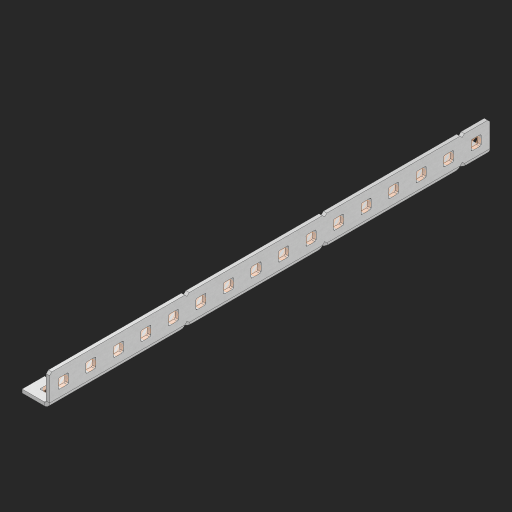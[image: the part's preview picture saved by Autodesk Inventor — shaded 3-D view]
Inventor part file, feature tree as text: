
AUTODESK INVENTOR PART (.ipt)
format: ipt  version: 2023 (Build 270158000, 158)  size: 883,712 bytes
history: native  units: in
note: dims shown in document units (in); Inventor stores cm internally (conversion verified against a paired STEP export)
features: other x196, extrude x46, sheet_metal_op x11, sketch x10, pattern_linear x2, mirror x1, chamfer x1
ambient origin geometry x8: Origin, YZ Plane, XZ Plane, XY Plane, X Axis, Y Axis, Z Axis, Center Point
bodies: Solid1 (feature_tree), Body (feature_tree)
feature tree (267):
  other  "Alu Half C 1x2x1x16"
  other  "Table"
  other  "Alu C 1x2x1x35"
  other  "Alu C 1x2x1x34"
  other  "Alu C 1x2x1x33"
  other  "Alu C 1x2x1x32"
  other  "Alu C 1x2x1x31"
  other  "Alu C 1x2x1x30"
  other  "Alu C 1x2x1x29"
  other  "Alu C 1x2x1x28"
  other  "Alu C 1x2x1x27"
  other  "Alu C 1x2x1x26"
  other  "Alu C 1x2x1x25"
  other  "Alu C 1x2x1x24"
  other  "Alu C 1x2x1x23"
  other  "Alu C 1x2x1x22"
  other  "Alu C 1x2x1x21"
  other  "Alu C 1x2x1x20"
  other  "Alu C 1x2x1x19"
  other  "Alu C 1x2x1x18"
  other  "Alu C 1x2x1x17"
  other  "Alu C 1x2x1x16"
  other  "Alu C 1x2x1x15"
  other  "Alu C 1x2x1x14"
  other  "Alu C 1x2x1x13"
  other  "Alu C 1x2x1x12"
  other  "Alu C 1x2x1x11"
  other  "Alu C 1x2x1x10"
  other  "Alu C 1x2x1x9"
  other  "Alu C 1x2x1x8"
  other  "Alu C 1x2x1x7"
  other  "Alu C 1x2x1x6"
  other  "Alu C 1x2x1x5"
  other  "Alu C 1x2x1x4"
  other  "Alu C 1x2x1x3"
  other  "Alu C 1x2x1x2"
  other  "Alu C 1x2x1x1"
  other  "Steel C 1x2x1x35"
  other  "Steel C 1x2x1x34"
  other  "Steel C 1x2x1x33"
  other  "Steel C 1x2x1x32"
  other  "Steel C 1x2x1x31"
  other  "Steel C 1x2x1x30"
  other  "Steel C 1x2x1x29"
  other  "Steel C 1x2x1x28"
  other  "Steel C 1x2x1x27"
  other  "Steel C 1x2x1x26"
  other  "Steel C 1x2x1x25"
  other  "Steel C 1x2x1x24"
  other  "Steel C 1x2x1x23"
  other  "Steel C 1x2x1x22"
  other  "Steel C 1x2x1x21"
  other  "Steel C 1x2x1x20"
  other  "Steel C 1x2x1x19"
  other  "Steel C 1x2x1x18"
  other  "Steel C 1x2x1x17"
  other  "Steel C 1x2x1x16"
  other  "Steel C 1x2x1x15"
  other  "Steel C 1x2x1x14"
  other  "Steel C 1x2x1x13"
  other  "Steel C 1x2x1x12"
  other  "Steel C 1x2x1x11"
  other  "Steel C 1x2x1x10"
  other  "Steel C 1x2x1x9"
  other  "Steel C 1x2x1x8"
  other  "Steel C 1x2x1x7"
  other  "Steel C 1x2x1x6"
  other  "Steel C 1x2x1x5"
  other  "Steel C 1x2x1x4"
  other  "Steel C 1x2x1x3"
  other  "Steel C 1x2x1x2"
  other  "Steel C 1x2x1x1"
  other  "Alu Half C 1x2x1x35"
  other  "Alu Half C 1x2x1x34"
  other  "Alu Half C 1x2x1x33"
  other  "Alu Half C 1x2x1x32"
  other  "Alu Half C 1x2x1x31"
  other  "Alu Half C 1x2x1x30"
  other  "Alu Half C 1x2x1x29"
  other  "Alu Half C 1x2x1x28"
  other  "Alu Half C 1x2x1x27"
  other  "Alu Half C 1x2x1x26"
  other  "Alu Half C 1x2x1x25"
  other  "Alu Half C 1x2x1x24"
  other  "Alu Half C 1x2x1x23"
  other  "Alu Half C 1x2x1x22"
  other  "Alu Half C 1x2x1x21"
  other  "Alu Half C 1x2x1x20"
  other  "Alu Half C 1x2x1x19"
  other  "Alu Half C 1x2x1x18"
  other  "Alu Half C 1x2x1x17"
  other  "Alu Half C 1x2x1x15"
  other  "Alu Half C 1x2x1x14"
  other  "Alu Half C 1x2x1x13"
  other  "Alu Half C 1x2x1x12"
  other  "Alu Half C 1x2x1x11"
  other  "Alu Half C 1x2x1x10"
  other  "Alu Half C 1x2x1x9"
  other  "Alu Half C 1x2x1x8"
  other  "Alu Half C 1x2x1x7"
  other  "Alu Half C 1x2x1x6"
  other  "Alu Half C 1x2x1x5"
  other  "Alu Half C 1x2x1x4"
  other  "Alu Half C 1x2x1x3"
  other  "Alu Half C 1x2x1x2"
  other  "Alu Half C 1x2x1x1"
  other  "Steel Half C 1x2x1x35"
  other  "Steel Half C 1x2x1x34"
  other  "Steel Half C 1x2x1x33"
  other  "Steel Half C 1x2x1x32"
  other  "Steel Half C 1x2x1x31"
  other  "Steel Half C 1x2x1x30"
  other  "Steel Half C 1x2x1x29"
  other  "Steel Half C 1x2x1x28"
  other  "Steel Half C 1x2x1x27"
  other  "Steel Half C 1x2x1x26"
  other  "Steel Half C 1x2x1x25"
  other  "Steel Half C 1x2x1x24"
  other  "Steel Half C 1x2x1x23"
  other  "Steel Half C 1x2x1x22"
  other  "Steel Half C 1x2x1x21"
  other  "Steel Half C 1x2x1x20"
  other  "Steel Half C 1x2x1x19"
  other  "Steel Half C 1x2x1x18"
  other  "Steel Half C 1x2x1x17"
  other  "Steel Half C 1x2x1x16"
  other  "Steel Half C 1x2x1x15"
  other  "Steel Half C 1x2x1x14"
  other  "Steel Half C 1x2x1x13"
  other  "Steel Half C 1x2x1x12"
  other  "Steel Half C 1x2x1x11"
  other  "Steel Half C 1x2x1x10"
  other  "Steel Half C 1x2x1x9"
  other  "Steel Half C 1x2x1x8"
  other  "Steel Half C 1x2x1x7"
  other  "Steel Half C 1x2x1x6"
  other  "Steel Half C 1x2x1x5"
  other  "Steel Half C 1x2x1x4"
  other  "Steel Half C 1x2x1x3"
  other  "Steel Half C 1x2x1x2"
  other  "Steel Half C 1x2x1x1"
  sheet_metal_op  "Flanges"
  other  "Flange Pattern Plane"
  other  "Flange Pattern Sketch"
  sheet_metal_op  "Flange Pattern"
  sheet_metal_op  "Body Pattern"
  pattern_linear  "Center Pattern"  Spacing1=0.0625in  [1 undecoded]
  other  "Arc Length"
  mirror  "Notch Mirror"
  pattern_linear  "Notch Pattern"  Spacing1=0.182in  [1 undecoded]
  chamfer  "End Chamfer"
  extrude  "Half Cut"  Depth=0.02in
  sketch  "Sketch1"  dims[d0=1.0in]
  other  "Plate1"
  sketch  "Sketch2"  dims[d1=8.0in]
  other  "Plate2"
  sheet_metal_op  "Bend1"
  sheet_metal_op  "Corner1"
  sketch  "Sketch3"  dims[d2=0.0625in]
  sketch  "Sketch7"  dims[d3=0.0625in]
  other  "Srf1"
  other  "Srf2"
  sketch  "Sketch8"  dims[d4=0.0312in]
  sketch  "Sketch9"  dims[d5=0.125in]
  other  "Srf91"
  sheet_metal_op  "Body Pattern Sketch"
  other  "Srf92"
  sketch  "Sketch13"  dims[d6=0.0625in]
  sketch  "Sketch14"  dims[d7=0.5in d8=90.0deg d9=0.0312in]
  sketch  "Sketch15"  dims[d10=0.25in]
  sketch  "Sketch16"  dims[d11=0.0625in d12=0.0625in d16=0.182in d17=0.02in d18=0.0625in d19=0.0in d20=0.25in d21=0.25in d38=6.2992in d40=0.5in d41=0.3937in d43=1.0in d46=0.172in d47=1.0in d48=0.0in d49=0.182in d50=0.02in d51=0.25in d52=0.25in d53=0.0625in d54=0.0in d55=0.172in d56=1.0in d57=0.0in d58=0.25in d60=6.2992in d62=0.5in d63=0.3937in d65=0.5in d85=0.1473in d86=0.1782in d88=0.04in d89=0.0625in d90=0.0in d91=0.04in d92=0.0491in d95=2.5in d96=0.04in d97=0.25in d98=45.0deg d99=0.25in d100=0.5in d101=0.0in d102=2.497in d106=0.182in d107=0.02in d108=0.5in d109=0.5in d110=0.0625in d111=0.0in d112=0.172in d113=0.5in d114=0.0in d117=0.5in d118=0.5in d119=0.5in]
  other  "Srf786"
  other  "Srf823"
  other  "Srf824"
  other  "Srf825"
  other  "Srf826"
  other  "Srf827"
  other  "Srf828"
  other  "Srf829"
  other  "Srf856"
  other  "Srf857"
  other  "Srf858"
  other  "Srf859"
  other  "Srf860"
  other  "Srf861"
  other  "Srf862"
  other  "Srf889"
  other  "Srf890"
  other  "Srf891"
  other  "Srf892"
  other  "Srf893"
  other  "Srf894"
  other  "Srf895"
  other  "Srf896"
  other  "Srf922"
  other  "Srf923"
  other  "Srf924"
  other  "Srf925"
  other  "Srf926"
  other  "Srf959"
  other  "Srf960"
  other  "Srf961"
  other  "Srf962"
  other  "Srf963"
  other  "Srf996"
  other  "Srf997"
  other  "Srf998"
  other  "Srf999"
  other  "Srf1000"
  other  "Srf1143"
  other  "Srf1144"
  other  "Srf1199"
  other  "Srf1200"
  other  "Srf1255"
  other  "Srf1256"
  sheet_metal_op  "Flange Stamp"
  sheet_metal_op  "Flange Circle"
  sheet_metal_op  "Body Stamp"
  sheet_metal_op  "Body Circle"
  other  "Center Stamp"
  other  "Center Circle"
  sheet_metal_op  "Notch"
  extrude  "ExtrusionSrf2"  Depth=0.0625in
  extrude  "ExtrusionSrf92"  TaperAngle=0.0deg  [1 undecoded]
  extrude  "ExtrusionSrf823"  Depth=0.25in
  extrude  "ExtrusionSrf824"  Depth=0.25in
  extrude  "ExtrusionSrf825"  Depth=0.5in
  extrude  "ExtrusionSrf826"  Depth=0.5in
  extrude  "ExtrusionSrf827"  Depth=1.0in TaperAngle=0.0deg
  extrude  "ExtrusionSrf828"  Depth=0.182in
  extrude  "ExtrusionSrf829"  Depth=0.02in
  extrude  "ExtrusionSrf856"  Depth=0.25in
  extrude  "ExtrusionSrf857"  Depth=0.25in
  extrude  "ExtrusionSrf858"  Depth=0.0625in
  extrude  "ExtrusionSrf859"  TaperAngle=0.0deg  [1 undecoded]
  extrude  "ExtrusionSrf860"  Depth=0.5in
  extrude  "ExtrusionSrf861"  Depth=1.0in TaperAngle=0.0deg
  extrude  "ExtrusionSrf862"  Depth=0.25in
  extrude  "ExtrusionSrf889"  Depth=0.5in
  extrude  "ExtrusionSrf890"  Depth=0.5in
  extrude  "ExtrusionSrf891"  Depth=0.5in
  extrude  "ExtrusionSrf892"  Depth=0.5in
  extrude  "ExtrusionSrf893"  Depth=0.5in
  extrude  "ExtrusionSrf894"  Depth=0.0625in
  extrude  "ExtrusionSrf895"  TaperAngle=0.0deg  [1 undecoded]
  extrude  "ExtrusionSrf896"  Depth=0.5in
  extrude  "ExtrusionSrf922"  Depth=0.5in
  extrude  "ExtrusionSrf923"  Depth=2.5in
  extrude  "ExtrusionSrf924"  Depth=0.25in TaperAngle=45.0deg
  extrude  "ExtrusionSrf925"  Depth=0.25in
  extrude  "ExtrusionSrf926"  Depth=0.5in TaperAngle=0.0deg
  extrude  "ExtrusionSrf959"  Depth=0.5in
  extrude  "ExtrusionSrf960"  Depth=0.182in
  extrude  "ExtrusionSrf961"  Depth=0.02in
  extrude  "ExtrusionSrf962"  Depth=0.5in
  extrude  "ExtrusionSrf963"  Depth=0.5in
  extrude  "ExtrusionSrf996"  Depth=0.0625in
  extrude  "ExtrusionSrf997"  TaperAngle=0.0deg  [1 undecoded]
  extrude  "ExtrusionSrf998"  Depth=0.5in
  extrude  "ExtrusionSrf999"  Depth=0.5in TaperAngle=0.0deg
  extrude  "ExtrusionSrf1000"  Depth=0.5in
  extrude  "ExtrusionSrf1143"  Depth=0.5in
  extrude  "ExtrusionSrf1144"  Depth=0.5in
  extrude  "ExtrusionSrf1199"  [1 undecoded]
  extrude  "ExtrusionSrf1200"  [1 undecoded]
  extrude  "ExtrusionSrf1255"  [1 undecoded]
  extrude  "ExtrusionSrf1256"  [1 undecoded]
note: 10 required parameter values undecoded (feature->parameter linkage not recoverable at this tier; creation-order binding heuristic only, values carry confidence <= 0.55)
